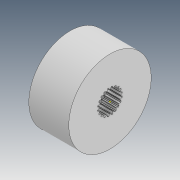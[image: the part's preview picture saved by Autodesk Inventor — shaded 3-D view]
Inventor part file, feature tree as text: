
AUTODESK INVENTOR PART (.ipt)
format: ipt  version: 2021 (Build 250183000, 183)  size: 294,400 bytes
history: native  units: in
note: dims shown in document units (in); Inventor stores cm internally (conversion verified against a paired STEP export)
features: sketch x4, extrude x3, other x2
ambient origin geometry x8: Origin, YZ Plane, XZ Plane, XY Plane, X Axis, Y Axis, Z Axis, Center Point
bodies: Body1 (feature_tree)
feature tree (9):
  other  "Sólido1"
  other  "Revolução1"
  extrude  "Extrusão1"  Depth=0.3858in
  extrude  "Extrusão2"  Depth=0.1378in
  extrude  "Extrusão5"  Depth=0.1909in
  sketch  "Esboço12"  dims[d7=0.0787in d8=0.0in d58=0.2008in d59=0.2323in d60=0.0024in d61=0.0024in d62=0.002in d63=0.002in d64=7.874in d66=360.0deg d68=0.1378in d69=0.0in]
  sketch  "Esboço2"  dims[d0=0.374in d1=0.3858in]
  sketch  "Esboço3"  dims[d2=90.0deg d3=0.1378in]
  sketch  "Esboço4"  dims[d4=0.1909in d5=0.0in d6=0.3543in]
